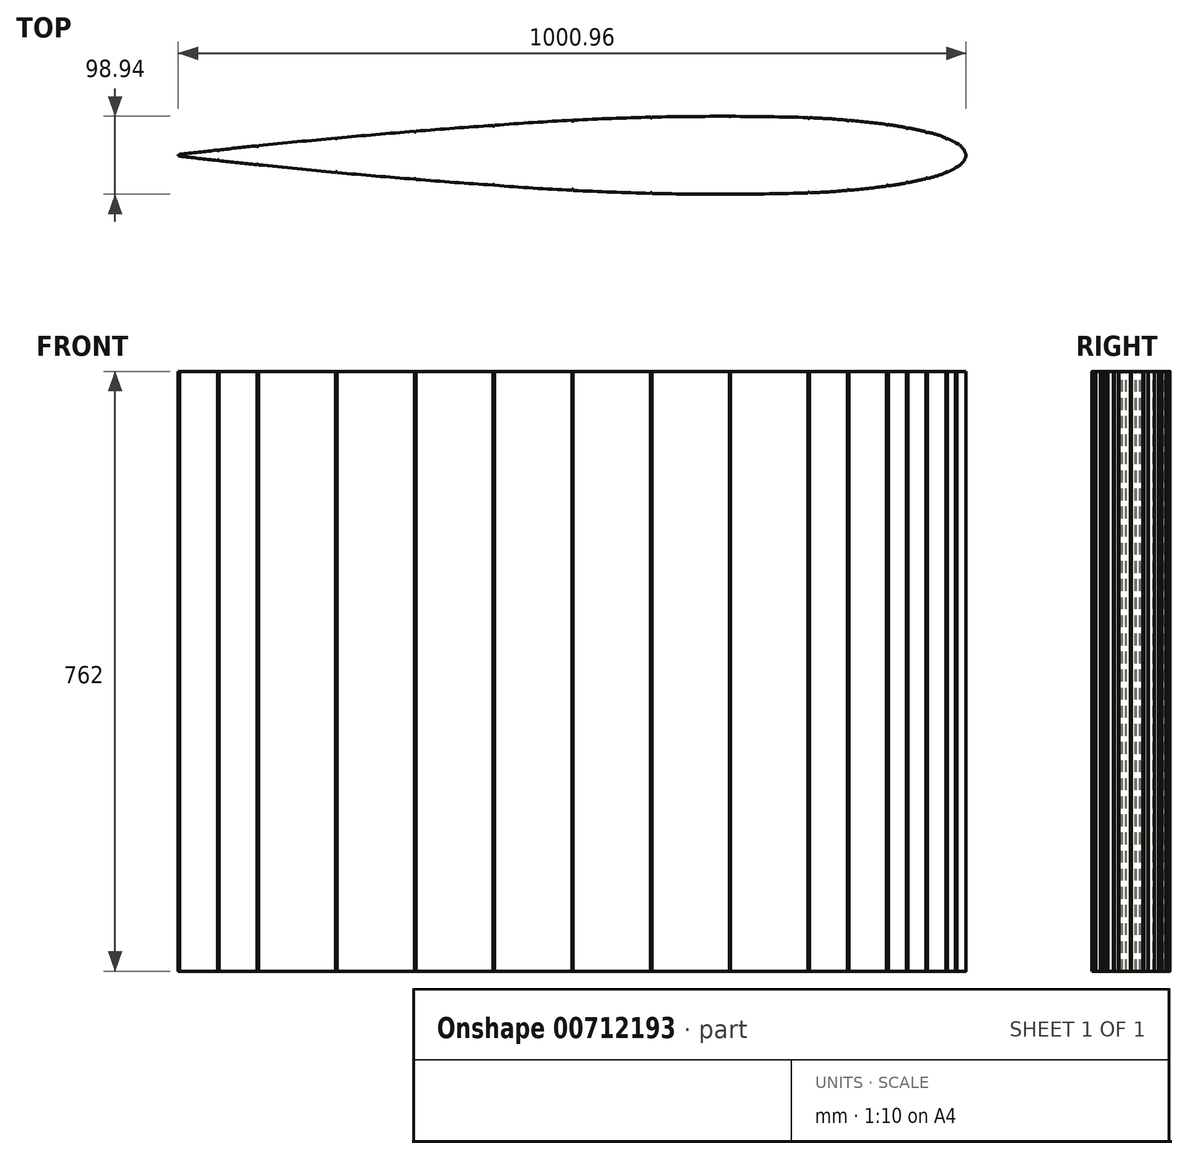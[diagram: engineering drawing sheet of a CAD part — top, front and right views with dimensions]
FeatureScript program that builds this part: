
annotation { "Feature Type Name" : "Feature", "Feature Type Description" : "" }
export const myFeature = defineFeature(function(context is Context, id is Id, definition is map)
    precondition{}
    {
        {
            var Q0;
            Q0=qCreatedBy(makeId("Top.planeOp"),FACE);
            var sketch = newSketch(context, id + "F0", { "sketchPlane" : qUnion([Q0])});
            skCircle(sketch, "E0", {"center": v(488, 15.78) * mm, "radius": 1 * mm});
            skCircle(sketch, "E1", {"center": v(475.5, 21.78) * mm, "radius": 1 * mm});
            skCircle(sketch, "E2", {"center": v(450.5, 29.62) * mm, "radius": 1 * mm});
            skCircle(sketch, "E3", {"center": v(425.5, 35) * mm, "radius": 1 * mm});
            skCircle(sketch, "E4", {"center": v(400.5, 39.02) * mm, "radius": 1 * mm});
            skCircle(sketch, "E5", {"center": v(350.5, 44.55) * mm, "radius": 1 * mm});
            skCircle(sketch, "E6", {"center": v(300.5, 47.82) * mm, "radius": 1 * mm});
            skCircle(sketch, "E7", {"center": v(200.5, 50.02) * mm, "radius": 1 * mm});
            skCircle(sketch, "E8", {"center": v(100.5, 48.37) * mm, "radius": 1 * mm});
            skCircle(sketch, "E9", {"center": v(0.5, 44.12) * mm, "radius": 1 * mm});
            skCircle(sketch, "E10", {"center": v(-99.5, 38.03) * mm, "radius": 1 * mm});
            skCircle(sketch, "E11", {"center": v(-199.5, 30.53) * mm, "radius": 1 * mm});
            skCircle(sketch, "E12", {"center": v(-299.5, 21.87) * mm, "radius": 1 * mm});
            skCircle(sketch, "E13", {"center": v(-399.5, 12.07) * mm, "radius": 1 * mm});
            skCircle(sketch, "E14", {"center": v(-449.5, 6.72) * mm, "radius": 1 * mm});
            skCircle(sketch, "E15", {"center": v(-499.5, 1.05) * mm, "radius": 1 * mm});
            skArc(sketch, "E16", {"start": v(-99.5, 38.03) * mm, "mid": v(-299.71, 21.85) * mm, "end": v(-499.5, 1.1) * mm});
            skArc(sketch, "E17", {"start": v(300.5, 47.82) * mm, "mid": v(100.37, 48.37) * mm, "end": v(-99.5, 38.03) * mm});
            skArc(sketch, "E18", {"start": v(400.5, 39.02) * mm, "mid": v(350.6, 44.54) * mm, "end": v(300.5, 47.82) * mm});
            skArc(sketch, "E19", {"start": v(450.5, 29.62) * mm, "mid": v(425.62, 34.98) * mm, "end": v(400.5, 39.02) * mm});
            skArc(sketch, "E20", {"start": v(488, 15.78) * mm, "mid": v(469.75, 24.05) * mm, "end": v(450.5, 29.62) * mm});
            skArc(sketch, "E21", {"start": v(500.38, 0.69) * mm, "mid": v(495.7, 9.48) * mm, "end": v(488, 15.78) * mm});
            skArc(sketch, "E22", {"start": v(500.5, 0) * mm, "mid": v(500.47, 0.35) * mm, "end": v(500.38, 0.69) * mm});
            skCircle(sketch, "E23", {"center": v(488, -15.78) * mm, "radius": 1 * mm});
            skCircle(sketch, "E24", {"center": v(475.5, -21.78) * mm, "radius": 1 * mm});
            skCircle(sketch, "E25", {"center": v(450.5, -29.62) * mm, "radius": 1 * mm});
            skCircle(sketch, "E26", {"center": v(425.5, -35) * mm, "radius": 1 * mm});
            skCircle(sketch, "E27", {"center": v(400.5, -39.02) * mm, "radius": 1 * mm});
            skCircle(sketch, "E28", {"center": v(350.5, -44.55) * mm, "radius": 1 * mm});
            skCircle(sketch, "E29", {"center": v(300.5, -47.82) * mm, "radius": 1 * mm});
            skCircle(sketch, "E30", {"center": v(200.5, -50.02) * mm, "radius": 1 * mm});
            skCircle(sketch, "E31", {"center": v(100.5, -48.37) * mm, "radius": 1 * mm});
            skCircle(sketch, "E32", {"center": v(0.5, -44.12) * mm, "radius": 1 * mm});
            skCircle(sketch, "E33", {"center": v(-99.5, -38.03) * mm, "radius": 1 * mm});
            skCircle(sketch, "E34", {"center": v(-199.5, -30.53) * mm, "radius": 1 * mm});
            skCircle(sketch, "E35", {"center": v(-299.5, -21.87) * mm, "radius": 1 * mm});
            skCircle(sketch, "E36", {"center": v(-399.5, -12.07) * mm, "radius": 1 * mm});
            skCircle(sketch, "E37", {"center": v(-449.5, -6.72) * mm, "radius": 1 * mm});
            skCircle(sketch, "E38", {"center": v(-499.5, -1.05) * mm, "radius": 1 * mm});
            skArc(sketch, "E39", {"start": v(-499.5, -1.1) * mm, "mid": v(-299.71, -21.85) * mm, "end": v(-99.5, -38.03) * mm});
            skArc(sketch, "E40", {"start": v(-99.5, -38.03) * mm, "mid": v(100.37, -48.37) * mm, "end": v(300.5, -47.82) * mm});
            skArc(sketch, "E41", {"start": v(300.5, -47.82) * mm, "mid": v(350.6, -44.54) * mm, "end": v(400.5, -39.02) * mm});
            skArc(sketch, "E42", {"start": v(400.5, -39.02) * mm, "mid": v(425.62, -34.98) * mm, "end": v(450.5, -29.62) * mm});
            skArc(sketch, "E43", {"start": v(450.5, -29.62) * mm, "mid": v(469.75, -24.05) * mm, "end": v(488, -15.78) * mm});
            skArc(sketch, "E44", {"start": v(488, -15.78) * mm, "mid": v(495.7, -9.48) * mm, "end": v(500.38, -0.69) * mm});
            skArc(sketch, "E45", {"start": v(500.38, -0.69) * mm, "mid": v(500.47, -0.35) * mm, "end": v(500.5, 0) * mm});
            skArc(sketch, "E46", {"start": v(-499.5, 1.1) * mm, "mid": v(-500.46, 0) * mm, "end": v(-499.5, -1.1) * mm});
            skSolve(sketch);
        }
        {
            var Q0;
            {var subQ7=sQuery(id+"F0.wireOp",EDGE,"E22");Q0=makeQuery(id+"F0.imprint","IMPRINT",FACE,{"disambiguationData":[TD([[makeQuery(id+"F0.imprint","IMPRINT",EDGE,{"derivedFrom":subQ7}),1.0]])]});}
            extrude(context, id + "F1", {"entities" : qUnion([Q0]), "oppositeDirection" : true, "depth" : 762 * mm, "offsetDistance" : 25.4 * mm});
        }
    });
